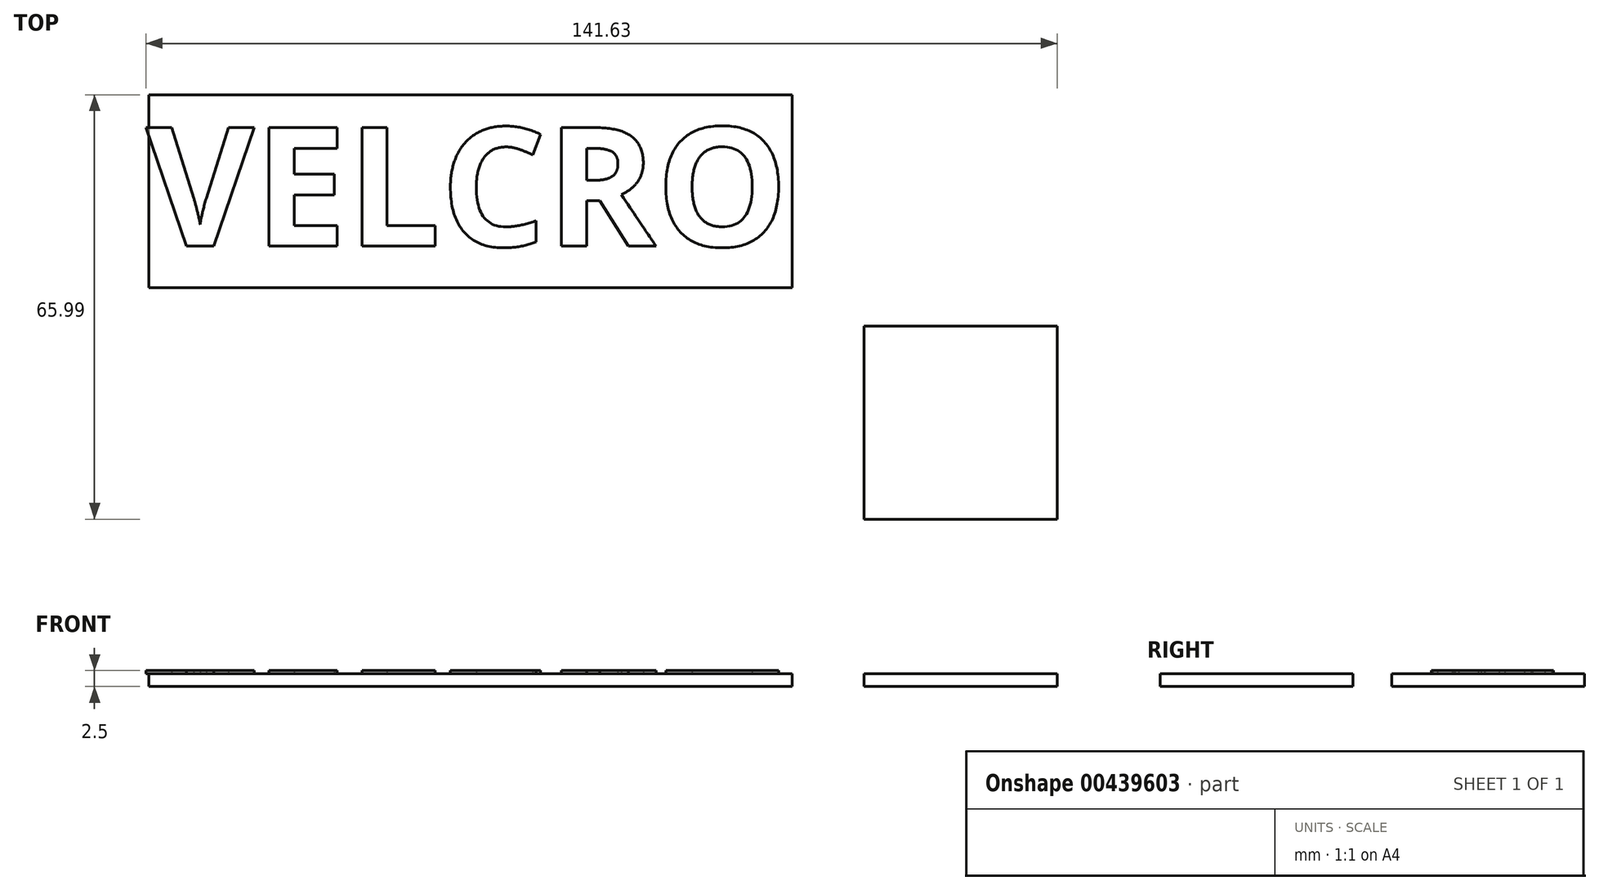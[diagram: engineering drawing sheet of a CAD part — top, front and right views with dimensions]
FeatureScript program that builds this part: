
annotation { "Feature Type Name" : "Feature", "Feature Type Description" : "" }
export const myFeature = defineFeature(function(context is Context, id is Id, definition is map)
    precondition{}
    {
        {
            var Q0;
            Q0=qCreatedBy(makeId("Top.planeOp"),FACE);
            var sketch = newSketch(context, id + "F0", { "sketchPlane" : qUnion([Q0])});
            skLineSegment(sketch, "E0.bottom", {"start": v(-15, 15) * mm, "end": v(15, 15) * mm});
            skLineSegment(sketch, "E0.top", {"start": v(-15, -15) * mm, "end": v(15, -15) * mm});
            skLineSegment(sketch, "E0.left", {"start": v(-15, 15) * mm, "end": v(-15, -15) * mm});
            skLineSegment(sketch, "E0.right", {"start": v(15, 15) * mm, "end": v(15, -15) * mm});
            skPoint(sketch, "E0.middle", {"position": v(0, 0) * mm});
            skLineSegment(sketch, "E1.bottom", {"start": v(-126.2, 50.99) * mm, "end": v(-26.2, 50.99) * mm});
            skLineSegment(sketch, "E1.top", {"start": v(-126.2, 20.99) * mm, "end": v(-26.2, 20.99) * mm});
            skLineSegment(sketch, "E1.left", {"start": v(-126.2, 50.99) * mm, "end": v(-126.2, 20.99) * mm});
            skLineSegment(sketch, "E1.right", {"start": v(-26.2, 50.99) * mm, "end": v(-26.2, 20.99) * mm});
            skSolve(sketch);
        }
        {
            var Q0;
            Q0 = qSketchRegion(id + "F0", true);
            extrude(context, id + "F1", {"entities" : qUnion([Q0]), "depth" : 2 * mm, "offsetDistance" : 25 * mm});
        }
        {
            var Q0;
            Q0=makeQuery(id+"F1.opExtrude","CAP_FACE",FACE,{"disambiguationData":[OSD([sQuery(id+"F0.wireOp",EDGE,"E1.bottom"),sQuery(id+"F0.wireOp",EDGE,"E1.top"),sQuery(id+"F0.wireOp",EDGE,"E1.left"),sQuery(id+"F0.wireOp",EDGE,"E1.right")])],"isStart":false});
            var sketch = newSketch(context, id + "F2", { "sketchPlane" : qUnion([Q0])});
            skText(sketch, "E2", { "text": "VELCRO", "fontName": "OpenSans-Bold.ttf"});
            const initialGuessF2  = {"E2": [-0.12663, 0.02744, 1, 0, 0.01858]};
            skSetInitialGuess(sketch, initialGuessF2);
            skSolve(sketch);
        }
        {
            var Q0;
            Q0 = qSketchRegion(id + "F2", true);
            extrude(context, id + "F3", {"entities" : qUnion([Q0]), "operationType" : NewBodyOperationType.ADD, "depth" : .5 * mm, "offsetDistance" : 25 * mm});
        }
    });
